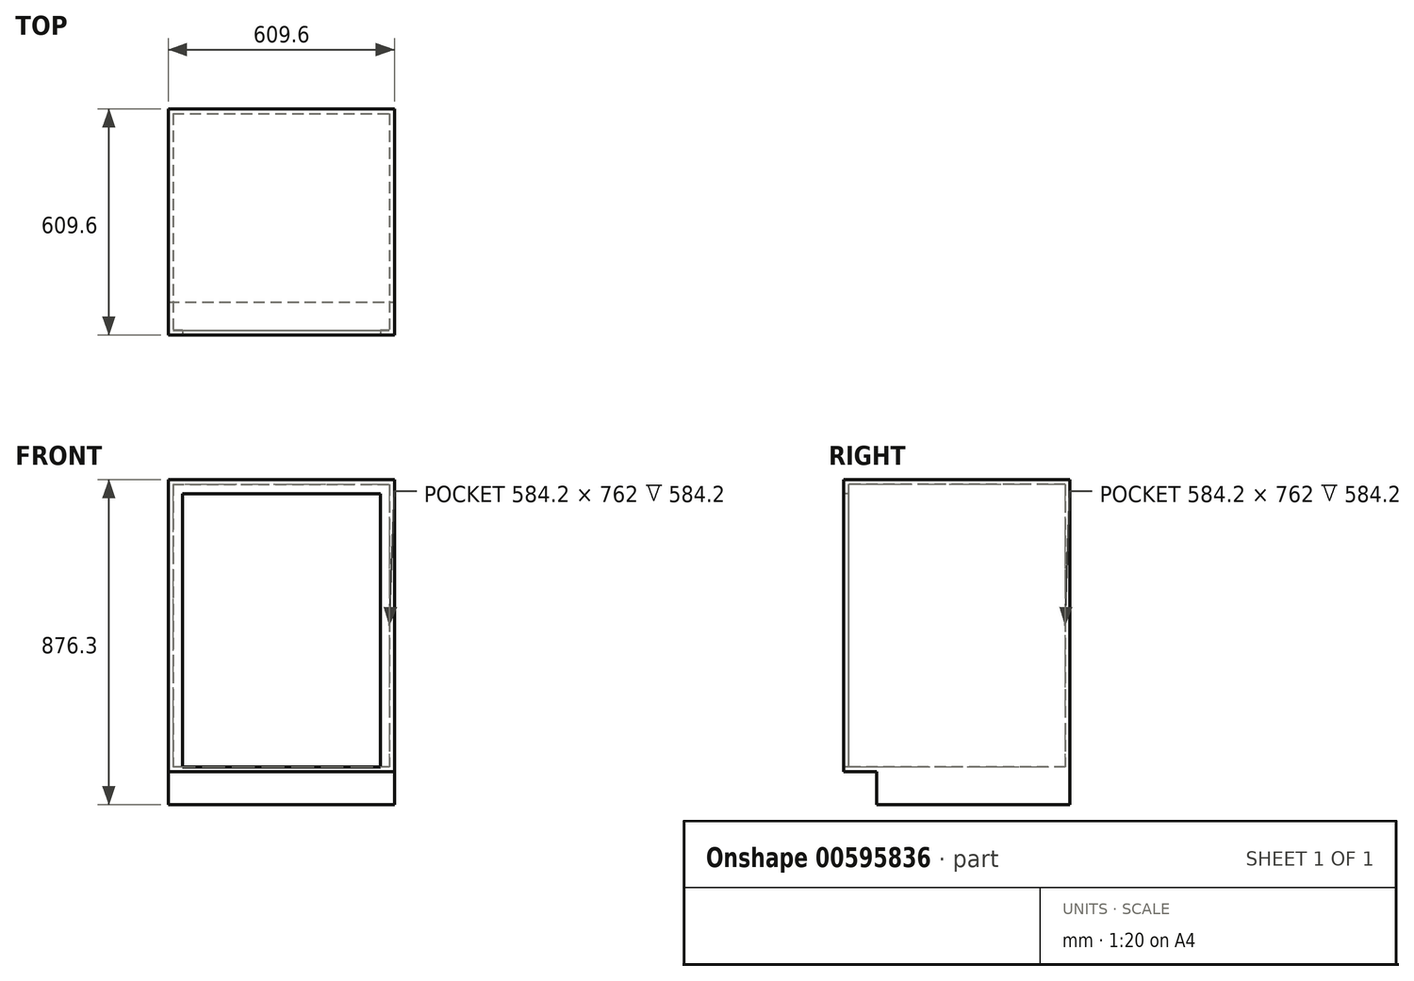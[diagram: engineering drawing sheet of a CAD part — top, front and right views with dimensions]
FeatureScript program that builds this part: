
annotation { "Feature Type Name" : "Feature", "Feature Type Description" : "" }
export const myFeature = defineFeature(function(context is Context, id is Id, definition is map)
    precondition{}
    {
        {
            var Q0;
            Q0=qCreatedBy(makeId("Top.planeOp"),FACE);
            var sketch = newSketch(context, id + "F0", { "sketchPlane" : qUnion([Q0])});
            skLineSegment(sketch, "E0.bottom", {"start": v(0, 0) * mm, "end": v(609.6, 0) * mm});
            skLineSegment(sketch, "E0.top", {"start": v(0, -609.6) * mm, "end": v(609.6, -609.6) * mm});
            skLineSegment(sketch, "E0.left", {"start": v(0, 0) * mm, "end": v(0, -609.6) * mm});
            skLineSegment(sketch, "E0.right", {"start": v(609.6, 0) * mm, "end": v(609.6, -609.6) * mm});
            skSolve(sketch);
        }
        {
            var Q0;
            Q0 = qSketchRegion(id + "F0", true);
            extrude(context, id + "F1", {"entities" : qUnion([Q0]), "depth" : 876.3 * mm, "offsetDistance" : 25.4 * mm});
        }
        {
            var Q0;
            Q0=makeQuery(id+"F1.opExtrude","SWEPT_FACE",FACE,{"disambiguationData":[OSD([sQuery(id+"F0.wireOp",EDGE,"E0.top")])]});
            var sketch = newSketch(context, id + "F2", { "sketchPlane" : qUnion([Q0])});
            skLineSegment(sketch, "E1.bottom", {"start": v(0, 0) * mm, "end": v(609.6, 0) * mm});
            skLineSegment(sketch, "E1.top", {"start": v(0, 88.9) * mm, "end": v(609.6, 88.9) * mm});
            skLineSegment(sketch, "E1.left", {"start": v(0, 0) * mm, "end": v(0, 88.9) * mm});
            skLineSegment(sketch, "E1.right", {"start": v(609.6, 0) * mm, "end": v(609.6, 88.9) * mm});
            skSolve(sketch);
        }
        {
            var Q0;
            Q0 = qSketchRegion(id + "F2", true);
            extrude(context, id + "F3", {"entities" : qUnion([Q0]), "operationType" : NewBodyOperationType.REMOVE, "oppositeDirection" : true, "depth" : 88.9 * mm, "offsetDistance" : 25.4 * mm});
        }
        {
            var Q0;
            Q0=makeQuery(id+"F1.opExtrude","SWEPT_FACE",FACE,{"disambiguationData":[OSD([sQuery(id+"F0.wireOp",EDGE,"E0.top")])]});
            shell(context, id + "F4", {"entities" : qUnion([Q0]), "thickness" : 12.7 * mm});
        }
        {
            var Q0;
            {var subQ0=sQuery(id+"F0.wireOp",EDGE,"E0.right");var subQ1=sQuery(id+"F0.wireOp",EDGE,"E0.left");var subQ2=sQuery(id+"F0.wireOp",EDGE,"E0.top");var subQ3=sQuery(id+"F0.wireOp",EDGE,"E0.bottom");Q0=makeQuery(id+"F4.opShell","OFFSET_FACE",FACE,{"disambiguationData":[OSD([subQ3,subQ2,subQ1,subQ0]),TDD([makeQuery(id+"F1.opExtrude","CAP_FACE",FACE,{"disambiguationData":[OSD([subQ3,subQ2,subQ1,subQ0])],"isStart":true})])]});}
            var Q1;
            Q1=makeQuery(id+"F4.opShell","OFFSET_FACE",FACE,{"disambiguationData":[OSD([sQuery(id+"F2.wireOp",EDGE,"E1.top")])]});
            extrude(context, id + "F5", {"entities" : qUnion([Q0]), "operationType" : NewBodyOperationType.ADD, "endBound" : BoundingType.UP_TO_SURFACE, "depth" : 25.4 * mm, "endBoundEntityFace" : qUnion([Q1]), "offsetDistance" : 25.4 * mm});
        }
        {
            var Q0;
            Q0=makeQuery(id+"F1.opExtrude","SWEPT_FACE",FACE,{"disambiguationData":[OSD([sQuery(id+"F0.wireOp",EDGE,"E0.top")])]});
            var sketch = newSketch(context, id + "F6", { "sketchPlane" : qUnion([Q0])});
            skLineSegment(sketch, "E2.0", {"start": v(38.1, 838.2) * mm, "end": v(571.5, 838.2) * mm});
            skLineSegment(sketch, "E2.1", {"start": v(38.1, 838.2) * mm, "end": v(38.1, 101.6) * mm});
            skLineSegment(sketch, "E2.3", {"start": v(571.5, 838.2) * mm, "end": v(571.5, 101.6) * mm});
            skSolve(sketch);
        }
        {
            var Q0;
            Q0=makeQuery(id+"F6.imprint","IMPRINT",FACE,{"disambiguationData":[TD([[makeQuery(id+"F6.imprint","IMPRINT",EDGE,{"derivedFrom":sQuery(id+"F6.wireOp",EDGE,"E2.0")}),1.0]])]});
            var Q1;
            {var subQ1=sQuery(id+"F0.wireOp",EDGE,"E0.top");Q1=makeQuery(id+"F6.imprint","IMPRINT",FACE,{"disambiguationData":[TD([[makeQuery(id+"F6.imprint","IMPRINT",EDGE,{"derivedFrom":makeQuery(id+"F1.opExtrude","CAP_EDGE",EDGE,{"disambiguationData":[OSD([subQ1])],"isStart":false})}),-1.0]])]});}
            extrude(context, id + "F7", {"entities" : qUnion([Q0, Q1]), "operationType" : NewBodyOperationType.ADD, "oppositeDirection" : true, "depth" : 12.7 * mm, "offsetDistance" : 25.4 * mm});
        }
    });
